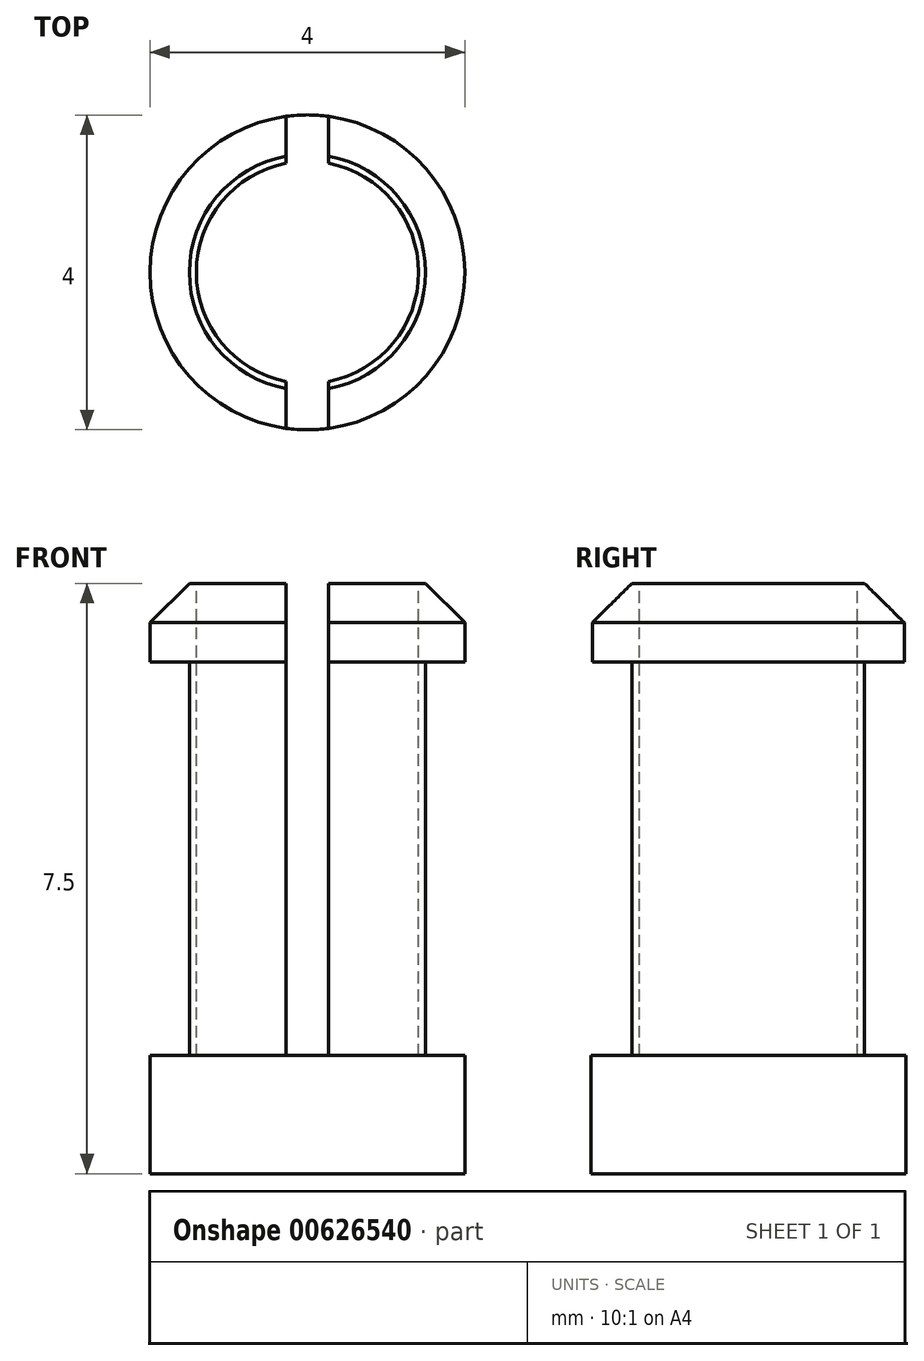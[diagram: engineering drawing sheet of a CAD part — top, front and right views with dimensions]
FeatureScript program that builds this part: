
annotation { "Feature Type Name" : "Feature", "Feature Type Description" : "" }
export const myFeature = defineFeature(function(context is Context, id is Id, definition is map)
    precondition{}
    {
        {
            var Q0;
            Q0=qCreatedBy(makeId("Top.planeOp"),FACE);
            var sketch = newSketch(context, id + "F0", { "sketchPlane" : qUnion([Q0])});
            skCircle(sketch, "E0", {"center": v(0, 0) * mm, "radius": 1.5 * mm});
            skSolve(sketch);
        }
        {
            var Q0;
            Q0=makeQuery(id+"F0.imprint","IMPRINT",FACE,{"disambiguationData":[TD([[makeQuery(id+"F0.imprint","IMPRINT",EDGE,{"derivedFrom":sQuery(id+"F0.wireOp",EDGE,"E0")}),1.0]])]});
            extrude(context, id + "F1", {"entities" : qUnion([Q0]), "depth" : 6 * mm, "offsetDistance" : 25 * mm});
        }
        {
            var Q0;
            Q0=makeQuery(id+"F1.opExtrude","CAP_FACE",FACE,{"disambiguationData":[OSD([sQuery(id+"F0.wireOp",EDGE,"E0")])],"isStart":false});
            var sketch = newSketch(context, id + "F2", { "sketchPlane" : qUnion([Q0])});
            skLineSegment(sketch, "E1.bottom", {"start": v(0.27, -2.13) * mm, "end": v(-0.27, -2.13) * mm});
            skLineSegment(sketch, "E1.top", {"start": v(0.27, 2.13) * mm, "end": v(-0.27, 2.13) * mm});
            skLineSegment(sketch, "E1.left", {"start": v(0.27, -2.13) * mm, "end": v(0.27, 2.13) * mm});
            skLineSegment(sketch, "E1.right", {"start": v(-0.27, -2.13) * mm, "end": v(-0.27, 2.13) * mm});
            skPoint(sketch, "E1.middle", {"position": v(0, 0) * mm});
            skCircle(sketch, "E2", {"center": v(0, 0) * mm, "radius": 2 * mm});
            skCircle(sketch, "E3", {"center": v(0, 0) * mm, "radius": 1.41 * mm});
            skSolve(sketch);
        }
        {
            var Q0;
            {var subQ0=sQuery(id+"F2.wireOp",EDGE,"E3");var subQ1=sQuery(id+"F2.wireOp",EDGE,"E1.left");var subQ2=makeQuery(id+"F2.imprint","INTERSECT",VERTEX,{"disambiguationData":[OD(0.0)],"derivedFrom":[subQ1,subQ0]});Q0=makeQuery(id+"F2.imprint","IMPRINT",FACE,{"disambiguationData":[TD([[makeQuery(id+"F2.imprint","IMPRINT",EDGE,{"disambiguationData":[TD([[subQ2,-1.0]])],"derivedFrom":subQ1}),1.0]])]});}
            var Q1;
            {var subQ0=sQuery(id+"F2.wireOp",EDGE,"E3");var subQ1=sQuery(id+"F2.wireOp",EDGE,"E1.left");var subQ2=makeQuery(id+"F2.imprint","INTERSECT",VERTEX,{"disambiguationData":[OD(0.0)],"derivedFrom":[subQ1,subQ0]});Q1=makeQuery(id+"F2.imprint","IMPRINT",FACE,{"disambiguationData":[TD([[makeQuery(id+"F2.imprint","IMPRINT",EDGE,{"disambiguationData":[TD([[subQ2,1.0]])],"derivedFrom":subQ1}),1.0]])]});}
            var Q2;
            {var subQ0=sQuery(id+"F2.wireOp",EDGE,"E3");var subQ1=sQuery(id+"F2.wireOp",EDGE,"E1.left");var subQ2=makeQuery(id+"F2.imprint","INTERSECT",VERTEX,{"disambiguationData":[OD(1.0)],"derivedFrom":[subQ1,subQ0]});Q2=makeQuery(id+"F2.imprint","IMPRINT",FACE,{"disambiguationData":[TD([[makeQuery(id+"F2.imprint","IMPRINT",EDGE,{"disambiguationData":[TD([[subQ2,-1.0]])],"derivedFrom":subQ1}),1.0]])]});}
            var Q3;
            {var subQ0=sQuery(id+"F2.wireOp",EDGE,"E3");var subQ1=sQuery(id+"F2.wireOp",EDGE,"E1.left");var subQ2=makeQuery(id+"F2.imprint","INTERSECT",VERTEX,{"disambiguationData":[OD(0.0)],"derivedFrom":[subQ1,subQ0]});Q3=makeQuery(id+"F2.imprint","IMPRINT",FACE,{"disambiguationData":[TD([[makeQuery(id+"F2.imprint","IMPRINT",EDGE,{"disambiguationData":[TD([[subQ2,-1.0]])],"derivedFrom":subQ1}),-1.0]])]});}
            var Q4;
            {var subQ0=sQuery(id+"F2.wireOp",EDGE,"E3");var subQ1=sQuery(id+"F2.wireOp",EDGE,"E1.right");var subQ2=makeQuery(id+"F2.imprint","INTERSECT",VERTEX,{"disambiguationData":[OD(0.0)],"derivedFrom":[subQ1,subQ0]});Q4=makeQuery(id+"F2.imprint","IMPRINT",FACE,{"disambiguationData":[TD([[makeQuery(id+"F2.imprint","IMPRINT",EDGE,{"disambiguationData":[TD([[subQ2,-1.0]])],"derivedFrom":subQ1}),1.0]])]});}
            extrude(context, id + "F3", {"entities" : qUnion([Q0, Q1, Q2, Q3, Q4]), "operationType" : NewBodyOperationType.REMOVE, "oppositeDirection" : true, "depth" : 8 * mm, "offsetDistance" : 25 * mm});
        }
        {
            var Q0;
            {var subQ0=sQuery(id+"F2.wireOp",EDGE,"E2");var subQ1=sQuery(id+"F2.wireOp",EDGE,"E1.left");var subQ2=makeQuery(id+"F2.imprint","INTERSECT",VERTEX,{"disambiguationData":[OD(0.0)],"derivedFrom":[subQ1,subQ0]});Q0=makeQuery(id+"F2.imprint","IMPRINT",FACE,{"disambiguationData":[TD([[makeQuery(id+"F2.imprint","IMPRINT",EDGE,{"disambiguationData":[TD([[subQ2,-1.0]])],"derivedFrom":subQ1}),-1.0]])]});}
            var Q1;
            {var subQ0=sQuery(id+"F2.wireOp",EDGE,"E2");var subQ1=sQuery(id+"F2.wireOp",EDGE,"E1.right");var subQ2=makeQuery(id+"F2.imprint","INTERSECT",VERTEX,{"disambiguationData":[OD(0.0)],"derivedFrom":[subQ1,subQ0]});Q1=makeQuery(id+"F2.imprint","IMPRINT",FACE,{"disambiguationData":[TD([[makeQuery(id+"F2.imprint","IMPRINT",EDGE,{"disambiguationData":[TD([[subQ2,-1.0]])],"derivedFrom":subQ1}),1.0]])]});}
            extrude(context, id + "F4", {"entities" : qUnion([Q0, Q1]), "operationType" : NewBodyOperationType.ADD, "oppositeDirection" : true, "depth" : 1 * mm, "offsetDistance" : 25 * mm});
        }
        {
            var Q0;
            Q0=makeQuery(id+"F1.opExtrude","CAP_FACE",FACE,{"disambiguationData":[OSD([sQuery(id+"F0.wireOp",EDGE,"E0")])],"isStart":true});
            var sketch = newSketch(context, id + "F5", { "sketchPlane" : qUnion([Q0])});
            skCircle(sketch, "E4", {"center": v(0, 0) * mm, "radius": 2 * mm});
            skSolve(sketch);
        }
        {
            var Q0;
            Q0=qSketchRegion(id+"F5",true);
            extrude(context, id + "F6", {"entities" : qUnion([Q0]), "operationType" : NewBodyOperationType.ADD, "depth" : 1.5 * mm, "offsetDistance" : 25 * mm});
        }
        {
            var Q0;
            {var subQ0=sQuery(id+"F2.wireOp",EDGE,"E2");var subQ1=sQuery(id+"F2.wireOp",EDGE,"E1.right");Q0=makeQuery(id+"F4.opExtrude","CAP_EDGE",EDGE,{"disambiguationData":[OSD([subQ0]),TDD([makeQuery(id+"F2.imprint","IMPRINT",EDGE,{"disambiguationData":[TD([[makeQuery(id+"F2.imprint","INTERSECT",VERTEX,{"disambiguationData":[OD(0.0)],"derivedFrom":[subQ1,subQ0]}),1.0]])],"derivedFrom":subQ0})])],"isStart":true});}
            var Q1;
            {var subQ0=sQuery(id+"F2.wireOp",EDGE,"E2");var subQ1=sQuery(id+"F2.wireOp",EDGE,"E1.left");Q1=makeQuery(id+"F4.opExtrude","CAP_EDGE",EDGE,{"disambiguationData":[OSD([subQ0]),TDD([makeQuery(id+"F2.imprint","IMPRINT",EDGE,{"disambiguationData":[TD([[makeQuery(id+"F2.imprint","INTERSECT",VERTEX,{"disambiguationData":[OD(0.0)],"derivedFrom":[subQ1,subQ0]}),-1.0]])],"derivedFrom":subQ0})])],"isStart":true});}
            chamfer(context, id + "F7", {"entities" : qUnion([Q0, Q1]), "width" : .5 * mm, "tangentPropagation" : true});
        }
    });
